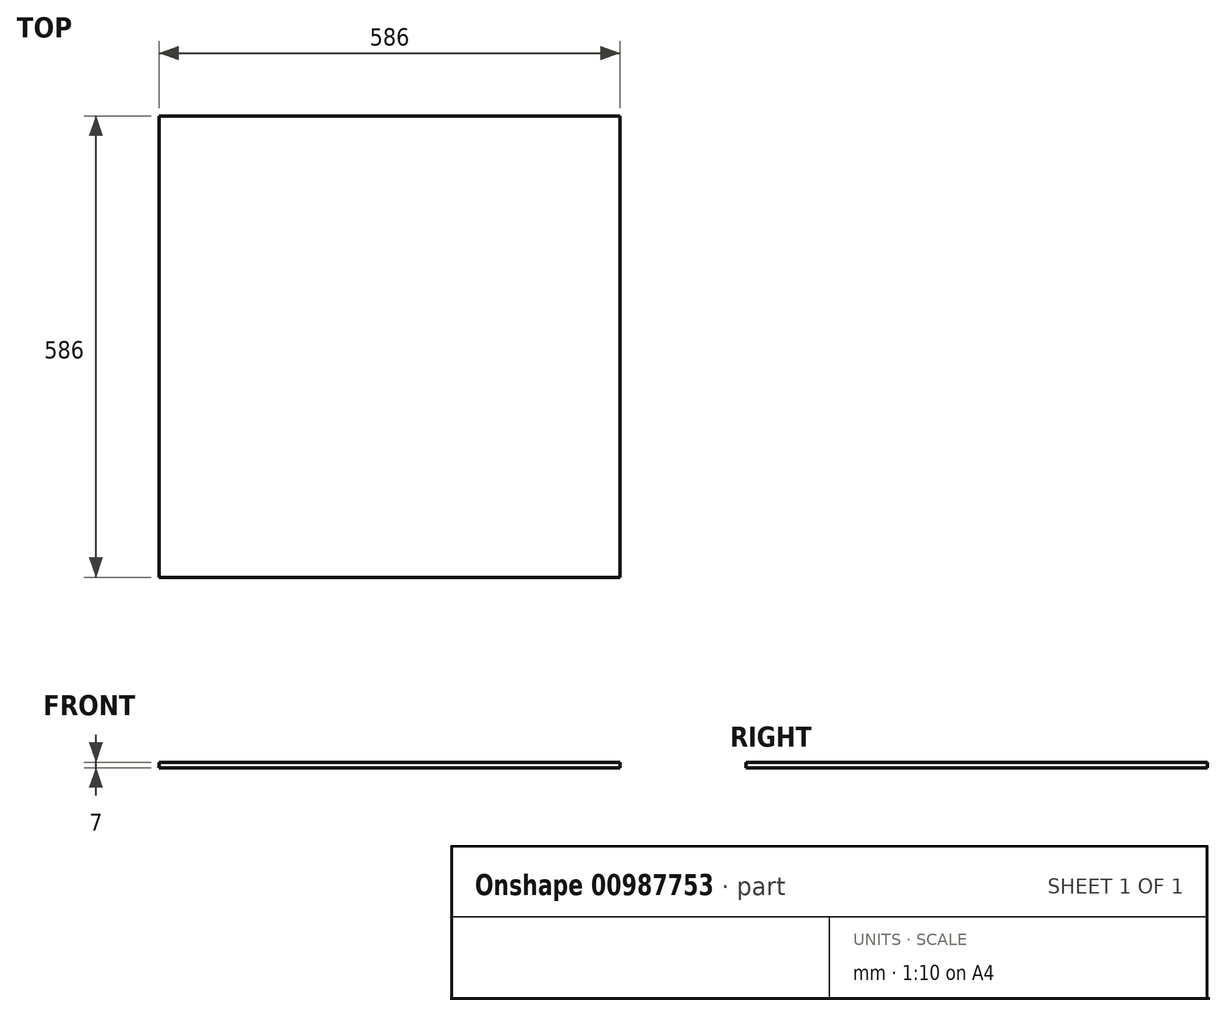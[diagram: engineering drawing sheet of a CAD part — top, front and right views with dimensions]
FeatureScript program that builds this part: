
annotation { "Feature Type Name" : "Feature", "Feature Type Description" : "" }
export const myFeature = defineFeature(function(context is Context, id is Id, definition is map)
    precondition{}
    {
        {
            var Q0;
            Q0=qCreatedBy(makeId("Top.planeOp"),FACE);
            var sketch = newSketch(context, id + "F0", { "sketchPlane" : qUnion([Q0])});
            skLineSegment(sketch, "E0.bottom", {"start": v(-293, 293) * mm, "end": v(293, 293) * mm});
            skLineSegment(sketch, "E0.top", {"start": v(-293, -293) * mm, "end": v(293, -293) * mm});
            skLineSegment(sketch, "E0.left", {"start": v(-293, 293) * mm, "end": v(-293, -293) * mm});
            skLineSegment(sketch, "E0.right", {"start": v(293, 293) * mm, "end": v(293, -293) * mm});
            skPoint(sketch, "E0.middle", {"position": v(0, 0) * mm});
            skSolve(sketch);
        }
        {
            var Q0;
            Q0=makeQuery(id+"F0.imprint","IMPRINT",FACE,{"disambiguationData":[TD([[makeQuery(id+"F0.imprint","IMPRINT",EDGE,{"derivedFrom":sQuery(id+"F0.wireOp",EDGE,"E0.bottom")}),-1.0]])]});
            extrude(context, id + "F1", {"entities" : qUnion([Q0]), "oppositeDirection" : true, "depth" : 7 * mm, "offsetDistance" : 25 * mm});
        }
    });
